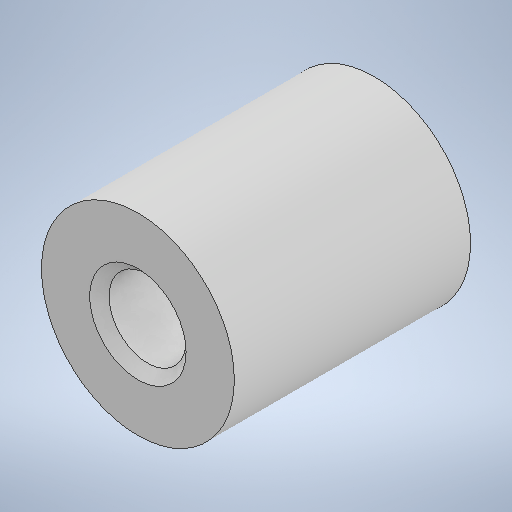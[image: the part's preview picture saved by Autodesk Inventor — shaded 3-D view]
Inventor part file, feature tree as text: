
AUTODESK INVENTOR PART (.ipt)
format: ipt  version: 2025.1 (Build 291241000, 241)  size: 203,264 bytes
history: native  units: in
note: dims shown in document units (in); Inventor stores cm internally (conversion verified against a paired STEP export)
features: extrude x1, chamfer x1, sketch x1
ambient origin geometry x8: Origin, YZ Plane, XZ Plane, XY Plane, X Axis, Y Axis, Z Axis, Center Point
bodies: Solid1 (feature_tree)
feature tree (3):
  extrude  "Extrusion1"  Depth=0.9646in
  chamfer  "Chamfer1"  Distance=0.9646in
  sketch  "Sketch1"  dims[d0=0.7874in d1=0.315in d2=0.9646in d3=0.0in d4=0.0394in d5=0.0787in d6=45.0deg]
